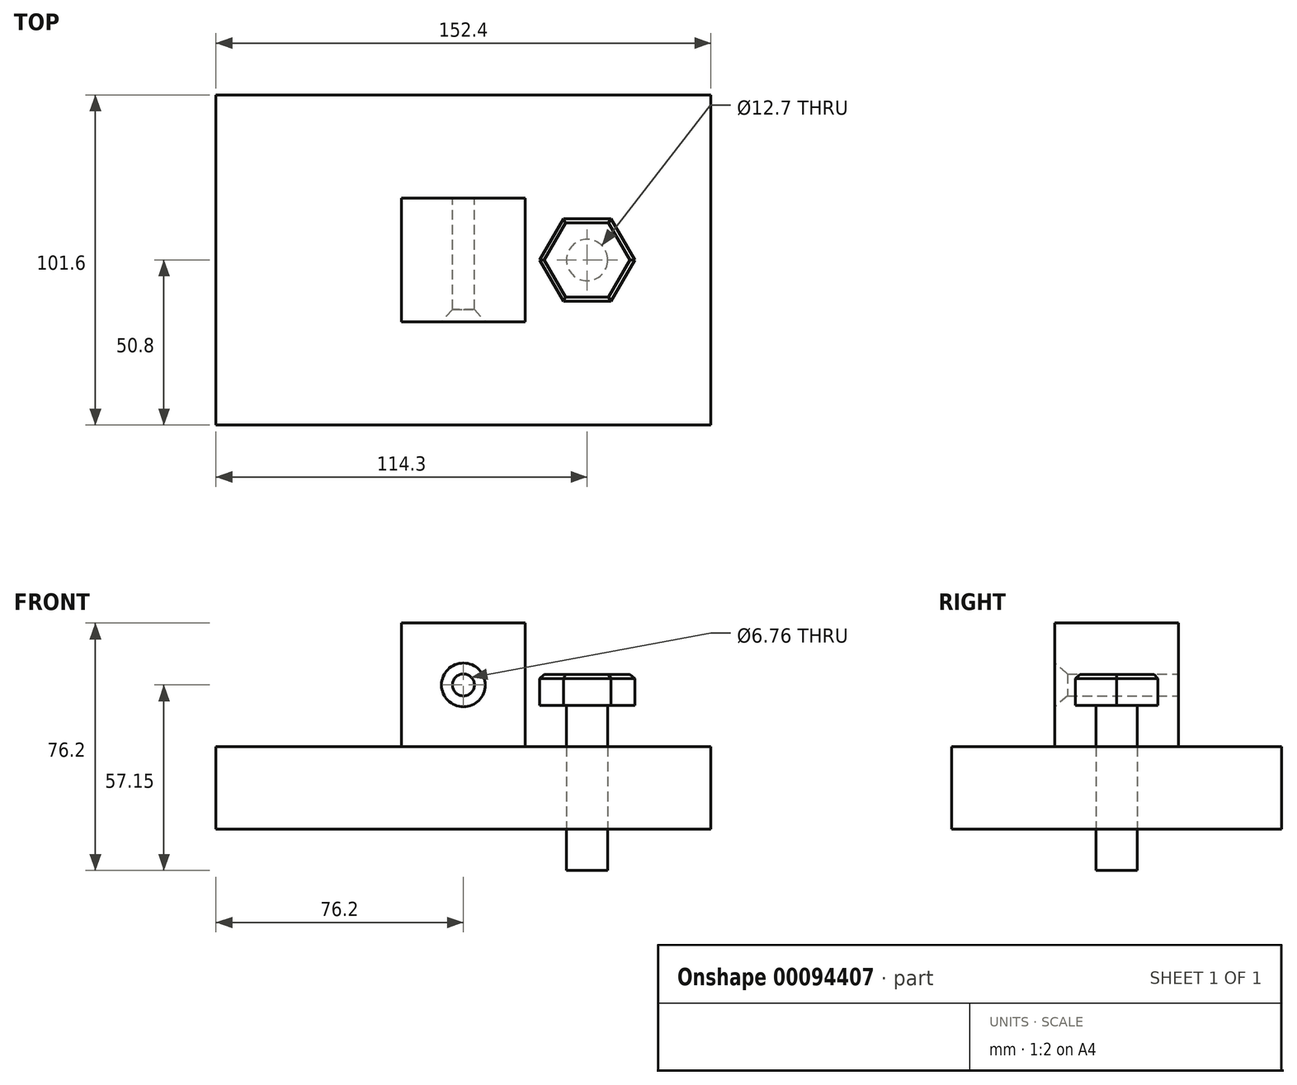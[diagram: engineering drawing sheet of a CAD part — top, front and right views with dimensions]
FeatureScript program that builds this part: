
annotation { "Feature Type Name" : "Feature", "Feature Type Description" : "" }
export const myFeature = defineFeature(function(context is Context, id is Id, definition is map)
    precondition{}
    {
        {
            var Q0;
            Q0=qCreatedBy(makeId("Top.planeOp"),FACE);
            var sketch = newSketch(context, id + "F0", { "sketchPlane" : qUnion([Q0])});
            skLineSegment(sketch, "E0.bottom", {"start": v(76.2, -50.8) * mm, "end": v(-76.2, -50.8) * mm});
            skLineSegment(sketch, "E0.top", {"start": v(76.2, 50.8) * mm, "end": v(-76.2, 50.8) * mm});
            skLineSegment(sketch, "E0.left", {"start": v(76.2, -50.8) * mm, "end": v(76.2, 50.8) * mm});
            skLineSegment(sketch, "E0.right", {"start": v(-76.2, -50.8) * mm, "end": v(-76.2, 50.8) * mm});
            skPoint(sketch, "E0.middle", {"position": v(0, 0) * mm});
            skLineSegment(sketch, "E1", {"start": v(0, 0) * mm, "end": v(76.2, 0) * mm, "construction": true});
            skCircle(sketch, "E2", {"center": v(38.1, 0) * mm, "radius": 6.35 * mm});
            skCircle(sketch, "E3.cCircle", {"center": v(38.1, 0) * mm, "radius": 12.7 * mm, "construction": true});
            skLineSegment(sketch, "E3.0", {"start": v(52.76, 0) * mm, "end": v(45.43, -12.7) * mm});
            skLineSegment(sketch, "E3.1", {"start": v(45.43, -12.7) * mm, "end": v(30.77, -12.7) * mm});
            skLineSegment(sketch, "E3.2", {"start": v(30.77, -12.7) * mm, "end": v(23.44, 0) * mm});
            skLineSegment(sketch, "E3.3", {"start": v(23.44, 0) * mm, "end": v(30.77, 12.7) * mm});
            skLineSegment(sketch, "E3.4", {"start": v(30.77, 12.7) * mm, "end": v(45.43, 12.7) * mm});
            skLineSegment(sketch, "E3.5", {"start": v(45.43, 12.7) * mm, "end": v(52.76, 0) * mm});
            skPoint(sketch, "E3.0.midPoint", {"position": v(49.1, -6.35) * mm});
            skSolve(sketch);
        }
        {
            var Q0;
            Q0=makeQuery(id+"F0.imprint","IMPRINT",FACE,{"disambiguationData":[TD([[makeQuery(id+"F0.imprint","IMPRINT",EDGE,{"derivedFrom":sQuery(id+"F0.wireOp",EDGE,"E0.bottom")}),-1.0]])]});
            var Q1;
            Q1=makeQuery(id+"F0.imprint","IMPRINT",FACE,{"disambiguationData":[TD([[makeQuery(id+"F0.imprint","IMPRINT",EDGE,{"derivedFrom":sQuery(id+"F0.wireOp",EDGE,"E2")}),-1.0]])]});
            extrude(context, id + "F1", {"entities" : qUnion([Q0, Q1]), "depth" : 25.4 * mm, "symmetric" : true});
        }
        {
            var Q0;
            Q0=makeQuery(id+"F1.opExtrude","CAP_FACE",FACE,{"disambiguationData":[OSD([sQuery(id+"F0.wireOp",EDGE,"E0.bottom"),sQuery(id+"F0.wireOp",EDGE,"E0.top"),sQuery(id+"F0.wireOp",EDGE,"E0.left"),sQuery(id+"F0.wireOp",EDGE,"E0.right")])],"isStart":false});
            var sketch = newSketch(context, id + "F2", { "sketchPlane" : qUnion([Q0])});
            skLineSegment(sketch, "E4.bottom", {"start": v(19.05, -19.05) * mm, "end": v(-19.05, -19.05) * mm});
            skLineSegment(sketch, "E4.top", {"start": v(19.05, 19.05) * mm, "end": v(-19.05, 19.05) * mm});
            skLineSegment(sketch, "E4.left", {"start": v(19.05, -19.05) * mm, "end": v(19.05, 19.05) * mm});
            skLineSegment(sketch, "E4.right", {"start": v(-19.05, -19.05) * mm, "end": v(-19.05, 19.05) * mm});
            skPoint(sketch, "E4.middle", {"position": v(0, 0) * mm});
            skSolve(sketch);
        }
        {
            var Q0;
            Q0 = qSketchRegion(id + "F2", true);
            extrude(context, id + "F3", {"entities" : qUnion([Q0]), "depth" : 38.1 * mm});
        }
        {
            var Q0;
            Q0=makeQuery(id+"F0.imprint","IMPRINT",FACE,{"disambiguationData":[TD([[makeQuery(id+"F0.imprint","IMPRINT",EDGE,{"derivedFrom":sQuery(id+"F0.wireOp",EDGE,"E2")}),1.0]])]});
            extrude(context, id + "F4", {"entities" : qUnion([Q0]), "depth" : 50.8 * mm, "symmetric" : true});
        }
        {
            var Q0;
            Q0=makeQuery(id+"F4.opExtrude","CAP_FACE",FACE,{"disambiguationData":[OSD([sQuery(id+"F0.wireOp",EDGE,"E2")])],"isStart":false});
            var sketch = newSketch(context, id + "F5", { "sketchPlane" : qUnion([Q0])});
            skSolve(sketch);
        }
        {
            var Q0;
            Q0=makeQuery(id+"F5.imprint","IMPRINT",FACE,{"disambiguationData":[TD([[makeQuery(id+"F5.imprint","IMPRINT",EDGE,{"derivedFrom":makeQuery(id+"F4.opExtrude","CAP_EDGE",EDGE,{"disambiguationData":[OSD([sQuery(id+"F0.wireOp",EDGE,"E2")])],"isStart":false})}),1.0]])]});
            var sketch = newSketch(context, id + "F6", { "sketchPlane" : qUnion([Q0])});
            skLineSegment(sketch, "E5.0", {"start": v(45.43, -12.7) * mm, "end": v(30.77, -12.7) * mm});
            skLineSegment(sketch, "E5.1", {"start": v(52.76, 0) * mm, "end": v(45.43, -12.7) * mm});
            skLineSegment(sketch, "E5.2", {"start": v(45.43, 12.7) * mm, "end": v(52.76, 0) * mm});
            skLineSegment(sketch, "E5.3", {"start": v(30.77, 12.7) * mm, "end": v(45.43, 12.7) * mm});
            skLineSegment(sketch, "E5.4", {"start": v(23.44, 0) * mm, "end": v(30.77, 12.7) * mm});
            skLineSegment(sketch, "E5.5", {"start": v(30.77, -12.7) * mm, "end": v(23.44, 0) * mm});
            skSolve(sketch);
        }
        {
            var Q0;
            Q0 = qSketchRegion(id + "F6", true);
            extrude(context, id + "F7", {"entities" : qUnion([Q0]), "operationType" : NewBodyOperationType.ADD, "depth" : 9.52 * mm});
        }
        {
            var Q0;
            Q0=makeQuery(id+"F7.opExtrude","CAP_FACE",FACE,{"disambiguationData":[OSD([sQuery(id+"F6.wireOp",EDGE,"E5.0"),sQuery(id+"F6.wireOp",EDGE,"E5.1"),sQuery(id+"F6.wireOp",EDGE,"E5.2"),sQuery(id+"F6.wireOp",EDGE,"E5.3"),sQuery(id+"F6.wireOp",EDGE,"E5.4"),sQuery(id+"F6.wireOp",EDGE,"E5.5")])],"isStart":false});
            chamfer(context, id + "F8", {"entities" : qUnion([Q0]), "width" : 1.27 * mm, "tangentPropagation" : true});
        }
        {
            var Q0;
            Q0=makeQuery(id+"F3.opExtrude","SWEPT_FACE",FACE,{"disambiguationData":[OSD([sQuery(id+"F2.wireOp",EDGE,"E4.bottom")])]});
            var sketch = newSketch(context, id + "F9", { "sketchPlane" : qUnion([Q0])});
            skPoint(sketch, "E6", {"position": v(0, 31.75) * mm});
            skPoint(sketch, "E6.positionSnap0", {"position": v(-19.05, 31.75) * mm});
            skSolve(sketch);
        }
        {
            var Q0;
            Q0=sQuery(id+"F9.wireOp",VERTEX,"E6");
            var Q1;
            Q1=makeQuery(id+"F3.opExtrude","SWEPT_BODY",BODY,{"disambiguationData":[OSD([sQuery(id+"F2.wireOp",EDGE,"E4.bottom"),sQuery(id+"F2.wireOp",EDGE,"E4.top"),sQuery(id+"F2.wireOp",EDGE,"E4.left"),sQuery(id+"F2.wireOp",EDGE,"E4.right")])]});
            hole(context, id + "F10", {"style" : HoleStyle.C_SINK, "endStyle" : HoleEndStyle.THROUGH, "standardTappedOrClearance" : lookupTablePath({ "standard" : "ANSI", "fit" : "Normal (ASME)", "size" : "1/4", "type" : "Clearance" }), "standardBlindInLast" : lookupTablePath({ "fit" : "Free", "standard" : "ANSI", "size" : "1/4", "type" : "Clearance" }), "holeDiameter" : 6.76 * mm, "cSinkDiameter" : 13.5 * mm, "cSinkAngle" : 82 * degree, "locations" : qUnion([Q0]), "scope" : qUnion([Q1]), "isTappedThrough" : true, "startStyle" : HoleStartStyle.PART});
        }
    });
